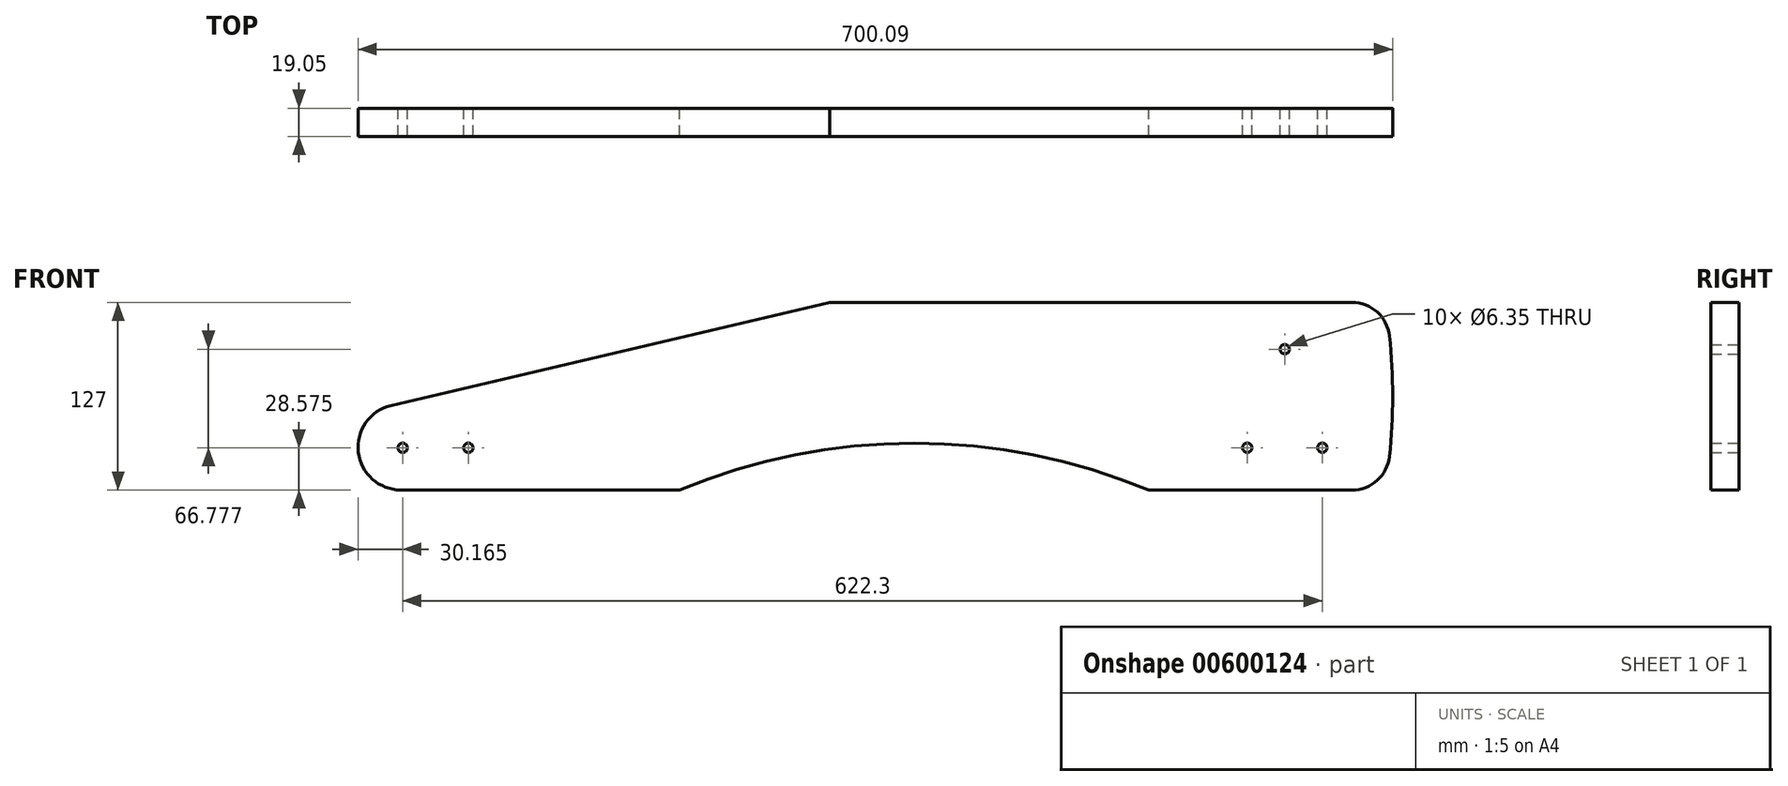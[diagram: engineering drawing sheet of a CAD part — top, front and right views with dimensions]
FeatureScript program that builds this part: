
annotation { "Feature Type Name" : "Feature", "Feature Type Description" : "" }
export const myFeature = defineFeature(function(context is Context, id is Id, definition is map)
    precondition{}
    {
        {
            var Q0;
            Q0=qCreatedBy(makeId("Front.planeOp"),FACE);
            var sketch = newSketch(context, id + "F0", { "sketchPlane" : qUnion([Q0])});
            skLineSegment(sketch, "E0.bottom", {"start": v(0, 0) * mm, "end": v(-700.09, 0) * mm, "construction": true});
            skLineSegment(sketch, "E0.top", {"start": v(0, 127) * mm, "end": v(-700.09, 127) * mm, "construction": true});
            skLineSegment(sketch, "E0.left", {"start": v(0, 0) * mm, "end": v(0, 127) * mm, "construction": true});
            skLineSegment(sketch, "E0.right", {"start": v(-700.09, 0) * mm, "end": v(-700.09, 127) * mm, "construction": true});
            skLineSegment(sketch, "E1", {"start": v(-27.45, 127) * mm, "end": v(-381, 127) * mm});
            skLineSegment(sketch, "E2", {"start": v(0, 63.5) * mm, "end": v(0, 63.5) * mm});
            skLineSegment(sketch, "E3", {"start": v(0, 63.5) * mm, "end": v(82, 63.5) * mm, "construction": true});
            skArc(sketch, "E4", {"start": v(-27.45, 127) * mm, "mid": v(-10.48, 120.5) * mm, "end": v(-2.2, 104.32) * mm});
            skArc(sketch, "E5.MirrorCS", {"start": v(-27.45, 0) * mm, "mid": v(-10.48, 6.5) * mm, "end": v(-2.2, 22.68) * mm});
            skArc(sketch, "E6", {"start": v(-2.2, 104.32) * mm, "mid": v(0, 63.5) * mm, "end": v(-2.2, 22.68) * mm});
            skLineSegment(sketch, "E7", {"start": v(-27.45, 0) * mm, "end": v(-165.1, 0) * mm});
            skLineSegment(sketch, "E8", {"start": v(-482.6, 0) * mm, "end": v(-671.13, 0) * mm});
            skArc(sketch, "E9", {"start": v(-165.1, 0) * mm, "mid": v(-323.85, 31.75) * mm, "end": v(-482.6, 0) * mm});
            skLineSegment(sketch, "E10", {"start": v(-323.85, 31.75) * mm, "end": v(-323.85, 0) * mm, "construction": true});
            skLineSegment(sketch, "E11", {"start": v(-381, 127) * mm, "end": v(-677.76, 57.15) * mm});
            skArc(sketch, "E12", {"start": v(-677.76, 57.15) * mm, "mid": v(-699.9, 25.62) * mm, "end": v(-671.13, 0) * mm});
            skLineSegment(sketch, "E13", {"start": v(-700.09, 28.57) * mm, "end": v(-669.93, 28.57) * mm, "construction": true});
            skLineSegment(sketch, "E14", {"start": v(-669.93, 28.57) * mm, "end": v(-625.48, 28.57) * mm, "construction": true});
            skCircle(sketch, "E15", {"center": v(-625.48, 28.57) * mm, "radius": 3.18 * mm});
            skCircle(sketch, "E16", {"center": v(-669.93, 28.57) * mm, "radius": 3.18 * mm});
            skLineSegment(sketch, "E17", {"start": v(-98.43, 28.63) * mm, "end": v(-47.62, 28.63) * mm, "construction": true});
            skLineSegment(sketch, "E18", {"start": v(-47.62, 28.63) * mm, "end": v(-28.57, 28.63) * mm, "construction": true});
            skLineSegment(sketch, "E19", {"start": v(-98.43, 28.63) * mm, "end": v(-117.48, 28.63) * mm, "construction": true});
            skLineSegment(sketch, "E20.bottom", {"start": v(-117.47, 38.2) * mm, "end": v(-28.58, 38.2) * mm, "construction": true});
            skLineSegment(sketch, "E20.top", {"start": v(-117.47, 19.05) * mm, "end": v(-28.58, 19.05) * mm, "construction": true});
            skLineSegment(sketch, "E20.left", {"start": v(-117.48, 38.2) * mm, "end": v(-117.48, 19.05) * mm, "construction": true});
            skLineSegment(sketch, "E20.right", {"start": v(-28.57, 38.2) * mm, "end": v(-28.57, 19.05) * mm, "construction": true});
            skPoint(sketch, "E21", {"position": v(-117.48, 28.63) * mm});
            skPoint(sketch, "E22", {"position": v(-28.57, 28.63) * mm});
            skLineSegment(sketch, "E23", {"start": v(-82.6, 38.2) * mm, "end": v(-82.6, 114.4) * mm, "construction": true});
            skLineSegment(sketch, "E24", {"start": v(-82.6, 114.4) * mm, "end": v(-63.45, 114.4) * mm, "construction": true});
            skLineSegment(sketch, "E25", {"start": v(-63.45, 114.4) * mm, "end": v(-63.45, 38.2) * mm, "construction": true});
            skPoint(sketch, "E26", {"position": v(-73.03, 114.4) * mm});
            skLineSegment(sketch, "E27", {"start": v(-73.03, 114.4) * mm, "end": v(-73.03, 95.35) * mm, "construction": true});
            skLineSegment(sketch, "E28", {"start": v(-73.03, 95.35) * mm, "end": v(-73.03, 38.2) * mm, "construction": true});
            skCircle(sketch, "E29", {"center": v(-98.43, 28.63) * mm, "radius": 3.17 * mm});
            skCircle(sketch, "E30", {"center": v(-47.62, 28.63) * mm, "radius": 3.17 * mm});
            skCircle(sketch, "E31", {"center": v(-73.03, 95.35) * mm, "radius": 3.17 * mm});
            skSolve(sketch);
        }
        {
            var Q0;
            Q0 = qSketchRegion(id + "F0", true);
            extrude(context, id + "F1", {"entities" : qUnion([Q0]), "depth" : 19.05 * mm, "offsetDistance" : 25.4 * mm});
        }
    });
